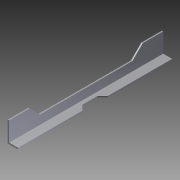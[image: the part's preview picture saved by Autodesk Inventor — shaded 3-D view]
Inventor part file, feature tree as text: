
AUTODESK INVENTOR PART (.ipt)
format: ipt  version: 2012 (Build 160160000, 160)  size: 101,376 bytes
history: native  units: in
note: dims shown in document units (in); Inventor stores cm internally (conversion verified against a paired STEP export)
features: extrude x3, sketch x3
ambient origin geometry x8: Origin, YZ Plane, XZ Plane, XY Plane, X Axis, Y Axis, Z Axis, Center Point
bodies: Solid1 (feature_tree)
feature tree (6):
  extrude  "Extrusion1"  Depth=0.9996in
  extrude  "Extrusion2"  Depth=0.125in
  extrude  "Extrusion3"  Depth=0.5in
  sketch  "Sketch1"  dims[d0=2.0in d1=0.9996in]
  sketch  "Sketch2"  dims[d2=0.125in d3=0.125in]
  sketch  "Sketch3"  dims[d4=15.0in d5=0.0in d6=0.5in d7=45.0deg d8=45.0deg d9=1.5in d10=6.75in d11=12.0in d12=0.0in d13=1.0in d14=45.0deg d15=45.0deg d16=2.0in d17=2.0in d18=12.0in d19=0.0in]
